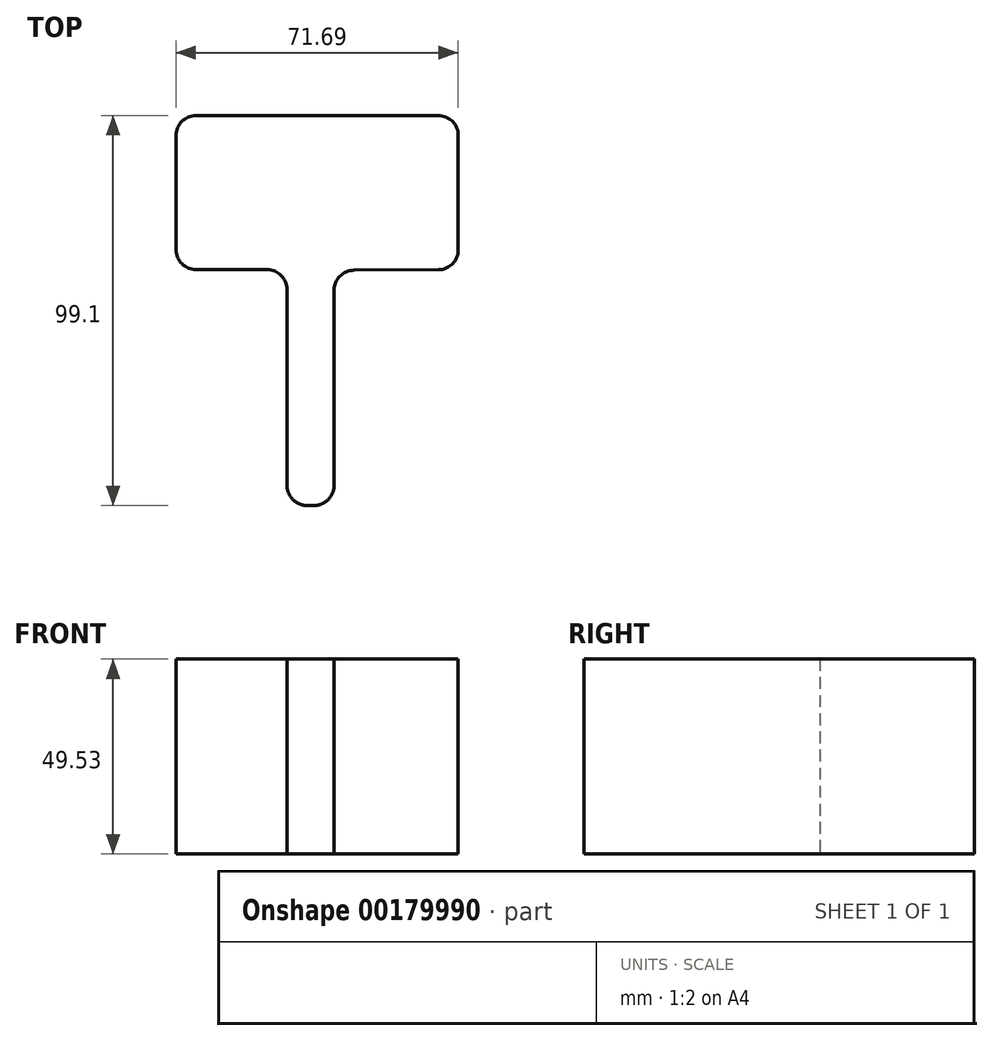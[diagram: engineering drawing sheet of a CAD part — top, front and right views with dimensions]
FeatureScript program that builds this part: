
annotation { "Feature Type Name" : "Feature", "Feature Type Description" : "" }
export const myFeature = defineFeature(function(context is Context, id is Id, definition is map)
    precondition{}
    {
        {
            var Q0;
            Q0=qCreatedBy(makeId("Top.planeOp"),FACE);
            var sketch = newSketch(context, id + "F0", { "sketchPlane" : qUnion([Q0])});
            skLineSegment(sketch, "E0", {"start": v(-30.36, 22.82) * mm, "end": v(-30.36, -32.02) * mm});
            skLineSegment(sketch, "E1", {"start": v(-30.36, -32.02) * mm, "end": v(-40.74, -37.12) * mm});
            skLineSegment(sketch, "E2", {"start": v(-40.74, -37.12) * mm, "end": v(-7.83, -37.12) * mm});
            skLineSegment(sketch, "E3", {"start": v(-7.83, -37.12) * mm, "end": v(-18.41, -32.02) * mm});
            skLineSegment(sketch, "E4", {"start": v(-18.41, -32.02) * mm, "end": v(-18.41, 22.62) * mm});
            skLineSegment(sketch, "E5", {"start": v(-30.36, 22.82) * mm, "end": v(-58.57, 22.82) * mm});
            skLineSegment(sketch, "E6", {"start": v(-58.57, 22.82) * mm, "end": v(-58.57, 61.98) * mm});
            skLineSegment(sketch, "E7", {"start": v(-58.57, 61.98) * mm, "end": v(13.12, 61.98) * mm});
            skLineSegment(sketch, "E8", {"start": v(13.12, 61.98) * mm, "end": v(13.12, 22.82) * mm});
            skLineSegment(sketch, "E9", {"start": v(13.12, 22.82) * mm, "end": v(-18.41, 22.62) * mm});
            skSolve(sketch);
        }
        {
            var Q0;
            Q0=makeQuery(id+"F0.imprint","IMPRINT",FACE,{"disambiguationData":[TD([[makeQuery(id+"F0.imprint","IMPRINT",EDGE,{"derivedFrom":sQuery(id+"F0.wireOp",EDGE,"E0")}),1.0]])]});
            extrude(context, id + "F1", {"entities" : qUnion([Q0]), "depth" : 49.53 * mm});
        }
        {
            var Q0;
            Q0=makeQuery(id+"F1.opExtrude","SWEPT_EDGE",EDGE,{"disambiguationData":[OSD([sQuery(id+"F0.wireOp",EDGE,"E2"),sQuery(id+"F0.wireOp",EDGE,"E3")])]});
            var Q1;
            Q1=makeQuery(id+"F1.opExtrude","SWEPT_EDGE",EDGE,{"disambiguationData":[OSD([sQuery(id+"F0.wireOp",EDGE,"E1"),sQuery(id+"F0.wireOp",EDGE,"E2")])]});
            var Q2;
            Q2=makeQuery(id+"F1.opExtrude","SWEPT_EDGE",EDGE,{"disambiguationData":[OSD([sQuery(id+"F0.wireOp",EDGE,"E8"),sQuery(id+"F0.wireOp",EDGE,"E9")])]});
            var Q3;
            Q3=makeQuery(id+"F1.opExtrude","SWEPT_EDGE",EDGE,{"disambiguationData":[OSD([sQuery(id+"F0.wireOp",EDGE,"E7"),sQuery(id+"F0.wireOp",EDGE,"E8")])]});
            var Q4;
            Q4=makeQuery(id+"F1.opExtrude","SWEPT_EDGE",EDGE,{"disambiguationData":[OSD([sQuery(id+"F0.wireOp",EDGE,"E5"),sQuery(id+"F0.wireOp",EDGE,"E6")])]});
            var Q5;
            Q5=makeQuery(id+"F1.opExtrude","SWEPT_EDGE",EDGE,{"disambiguationData":[OSD([sQuery(id+"F0.wireOp",EDGE,"E4"),sQuery(id+"F0.wireOp",EDGE,"E9")])]});
            var Q6;
            Q6=makeQuery(id+"F1.opExtrude","SWEPT_EDGE",EDGE,{"disambiguationData":[OSD([sQuery(id+"F0.wireOp",EDGE,"E6"),sQuery(id+"F0.wireOp",EDGE,"E7")])]});
            var Q7;
            Q7=makeQuery(id+"F1.opExtrude","SWEPT_EDGE",EDGE,{"disambiguationData":[OSD([sQuery(id+"F0.wireOp",EDGE,"E0"),sQuery(id+"F0.wireOp",EDGE,"E5")])]});
            fillet(context, id + "F2", {"entities" : qUnion([Q0, Q1, Q2, Q3, Q4, Q5, Q6, Q7]), "radius" : 5.08 * mm, "tangentPropagation" : true, "allowEdgeOverflow" : false});
        }
    });
